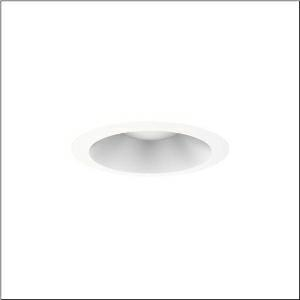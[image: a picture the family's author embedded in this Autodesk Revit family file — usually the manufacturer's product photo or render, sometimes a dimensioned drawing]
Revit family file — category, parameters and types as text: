
# Revit family: lunis_31-l_51dn16eg32b
name_source: partatom
category: Lighting Fixtures
units: mm (PartAtom-declared; Revit-internal decimal feet)

## family parameters
Cut with Voids When Loaded = No
Host = Face
Light Source = No
Part Type = Normal
Room Calculation Point = No
Round Connector Dimension = Use Diameter
Shared = No

## types (1)
- --- (1 x LED, 2500 lm, 17 W, 3000K)
    Apparent Load = 17 VA
    CIE Flux Codes = 64 93 99 100 100
    Color Rendering = 80
    Color Temperature = 3000K
    Default Elevation = 1800 mm
    Description = Lunis 31-L, downlight, light control with reflector, light emission: direct distribution, LED rated luminous flux: 2.500lm, light colour: 830, mains connection: 220..240V, AC/DC, 0/50..60Hz, housing, of aluminium, white, protection rating (complete): IP20, protection rating (on room side): IP54, insulation class (complete): insulation class II (safety insulation), certification: CE, ENEC, packaging unit: 1 piece
    Height = 0 mm  [stored 0 ft]
    Lamp = 1 x LED
    Lamp Light Flux = 2500 lm
    Lamp Power = 17 W
    Lamp count = 1
    Length = 259 mm
    Luminous efficacy = 147 lm/W
    Manufacturer = Siteco
    ModVariant = No
    Model = 51DN16EG32B
    Mounting Place = Ceiling
    Mounting Type = Recessed
    Number of Poles = 1
    OnlyDefault = Yes
    Power Factor = 1
    Product Name = Lunis 31-L
    Product group = downlight
    ProductGroupID = 401
    Protection Class = Protection class II
    Protection Degree = IP 20
    RLX_Detail_Level = 1
    RLX_Emergency_Light_Flux = 0 lm
    RLX_Emergency_Type = 0
    RLX_Emergency_Type_DB = No
    RlxData = <blob elided: 24301 chars, md5=d10de118>
    Socket = socket
    Standby Power = 0 W
    System Light Flux = 2500 lm
    System Power = 17 W
    Type Comments = individual setting: luminous flux: 100 % | (ON | OFF | ON) | 450 mA
    Type Image = l_1345915.jpg
    URL = http://relux.com
    VarID = @adj_029641
    Voltage = 0 V
    Weight = 0.00 kg
    Width = 0 mm  [stored 0 ft]

note: [stored X ft] marks values corroborated as IEEE doubles in the binary element streams (Revit-internal decimal feet)

## geometry (parser evidence)
native form markers: Blend x4, Sweep x10
no freeform markers — native parametric forms only
